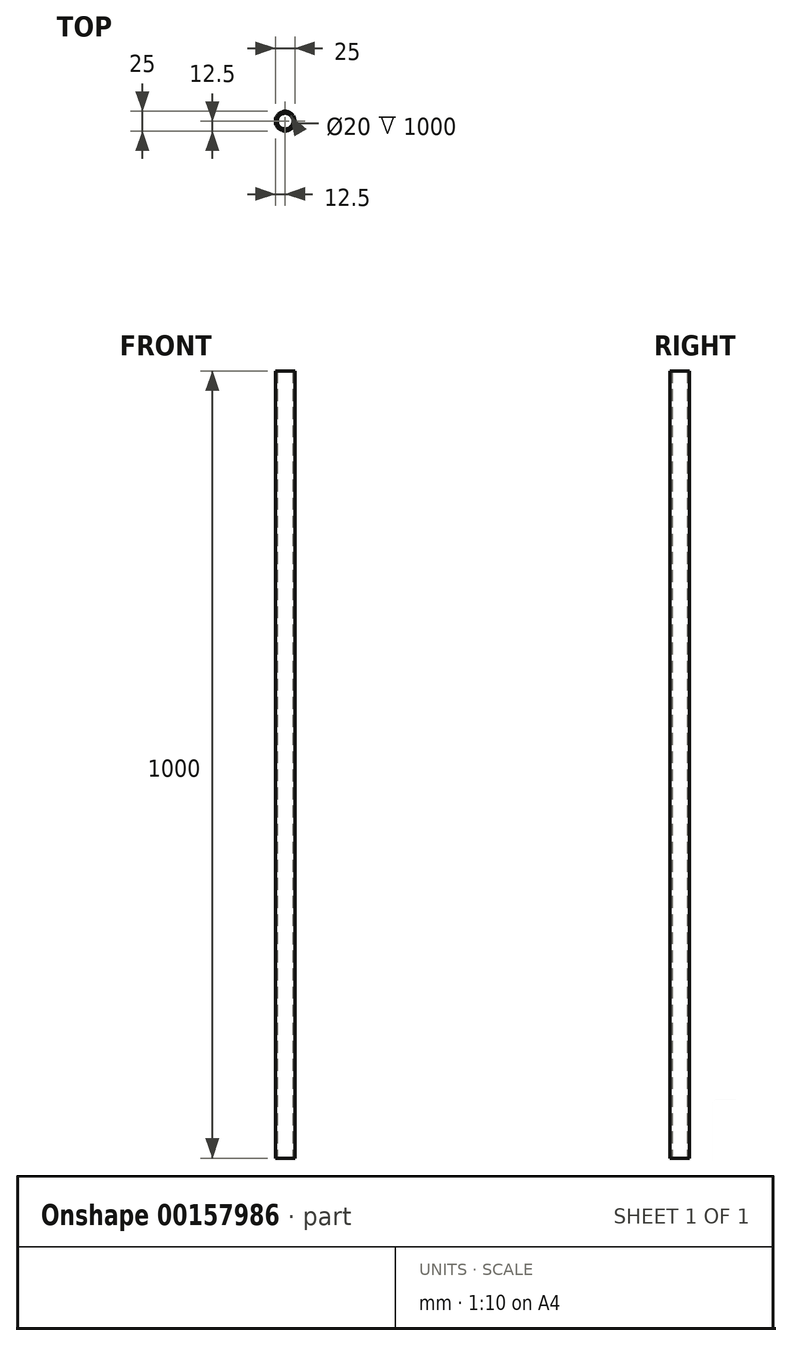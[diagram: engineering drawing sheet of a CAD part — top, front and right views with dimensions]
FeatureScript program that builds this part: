
annotation { "Feature Type Name" : "Feature", "Feature Type Description" : "" }
export const myFeature = defineFeature(function(context is Context, id is Id, definition is map)
    precondition{}
    {
        {
            var Q0;
            Q0=qCreatedBy(makeId("Top.planeOp"),FACE);
            var sketch = newSketch(context, id + "F0", { "sketchPlane" : qUnion([Q0])});
            skCircle(sketch, "E0", {"center": v(0, 0) * mm, "radius": 12.5 * mm});
            skCircle(sketch, "E1", {"center": v(0, 0) * mm, "radius": 10 * mm});
            skSolve(sketch);
        }
        {
            var Q0;
            Q0 = qSketchRegion(id + "F0", true);
            extrude(context, id + "F1", {"entities" : qUnion([Q0]), "depth" : 1000 * mm});
        }
    });
